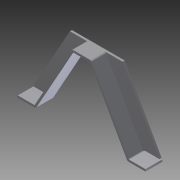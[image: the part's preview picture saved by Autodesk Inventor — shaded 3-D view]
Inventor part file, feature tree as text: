
AUTODESK INVENTOR PART (.ipt)
format: ipt  version: 2012 (Build 160160000, 160)  size: 121,856 bytes
history: native  units: in
note: dims shown in document units (in); Inventor stores cm internally (conversion verified against a paired STEP export)
features: extrude x2, fillet x2, sketch x1
ambient origin geometry x8: Origin, YZ Plane, XZ Plane, XY Plane, X Axis, Y Axis, Z Axis, Center Point
bodies: Solid1 (feature_tree)
feature tree (5):
  sketch  "Sketch1"  dims[d0=7.625in d1=1.0in d2=1.0in d3=1.0in d4=0.125in d5=0.125in d6=4.0in d7=0.0625in d8=0.0625in d9=0.0625in d10=1.0in d11=0.0in d12=0.125in d13=0.0in d14=0.0625in d15=0.125in]
  extrude  "Extrusion1"  Depth=1.0in
  extrude  "Extrusion2"  Depth=1.0in
  fillet  "Fillet1"  Radius=1.0in
  fillet  "Fillet2"  Radius=0.125in
